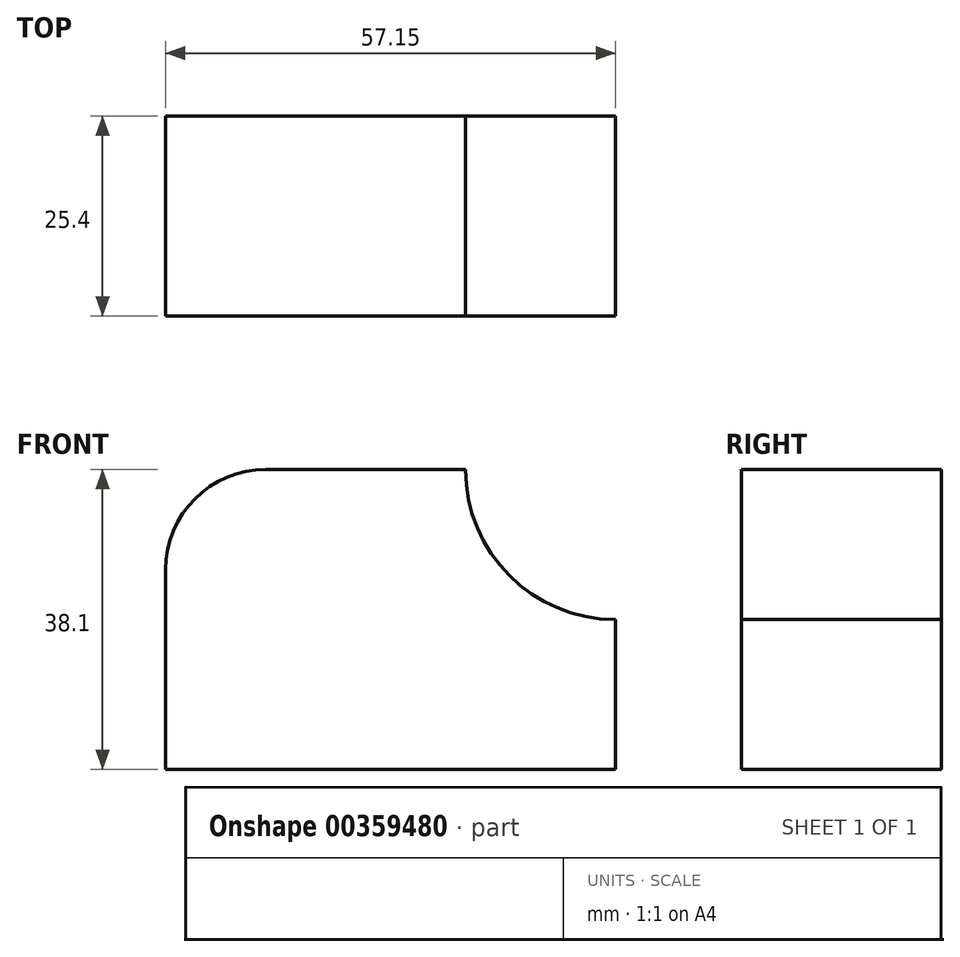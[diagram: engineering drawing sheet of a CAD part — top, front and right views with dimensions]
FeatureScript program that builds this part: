
annotation { "Feature Type Name" : "Feature", "Feature Type Description" : "" }
export const myFeature = defineFeature(function(context is Context, id is Id, definition is map)
    precondition{}
    {
        {
            var Q0;
            Q0=qCreatedBy(makeId("Front.planeOp"),FACE);
            var sketch = newSketch(context, id + "F0", { "sketchPlane" : qUnion([Q0])});
            skLineSegment(sketch, "E0", {"start": v(0, 38.1) * mm, "end": v(0, 0) * mm});
            skLineSegment(sketch, "E1", {"start": v(0, 0) * mm, "end": v(57.15, 0) * mm});
            skLineSegment(sketch, "E2", {"start": v(57.15, 0) * mm, "end": v(57.15, 38.1) * mm});
            skLineSegment(sketch, "E3", {"start": v(57.15, 38.1) * mm, "end": v(0, 38.1) * mm});
            skSolve(sketch);
        }
        {
            var Q0;
            Q0 = qSketchRegion(id + "F0", true);
            extrude(context, id + "F1", {"entities" : qUnion([Q0]), "oppositeDirection" : true, "depth" : 25.4 * mm});
        }
        {
            var Q0;
            Q0=qCreatedBy(makeId("Front.planeOp"),FACE);
            var sketch = newSketch(context, id + "F2", { "sketchPlane" : qUnion([Q0])});
            skArc(sketch, "E4", {"start": v(38.1, 38.1) * mm, "mid": v(43.68, 24.63) * mm, "end": v(57.15, 19.05) * mm});
            skLineSegment(sketch, "E5", {"start": v(38.1, 38.1) * mm, "end": v(57.15, 38.1) * mm});
            skLineSegment(sketch, "E6", {"start": v(57.15, 38.1) * mm, "end": v(57.15, 19.05) * mm});
            skSolve(sketch);
        }
        {
            var Q0;
            Q0 = qSketchRegion(id + "F2", true);
            extrude(context, id + "F3", {"entities" : qUnion([Q0]), "operationType" : NewBodyOperationType.REMOVE, "oppositeDirection" : true, "depth" : 25.4 * mm});
        }
        {
            var Q0;
            Q0=qCreatedBy(makeId("Front.planeOp"),FACE);
            var sketch = newSketch(context, id + "F4", { "sketchPlane" : qUnion([Q0])});
            skArc(sketch, "E7", {"start": v(12.7, 38.1) * mm, "mid": v(3.72, 34.38) * mm, "end": v(0, 25.4) * mm});
            skLineSegment(sketch, "E8", {"start": v(0, 25.4) * mm, "end": v(0, 38.1) * mm});
            skLineSegment(sketch, "E9", {"start": v(12.7, 38.1) * mm, "end": v(0, 38.1) * mm});
            skSolve(sketch);
        }
        {
            var Q0;
            Q0 = qSketchRegion(id + "F4", true);
            extrude(context, id + "F5", {"entities" : qUnion([Q0]), "operationType" : NewBodyOperationType.REMOVE, "oppositeDirection" : true, "depth" : 25.4 * mm});
        }
    });
